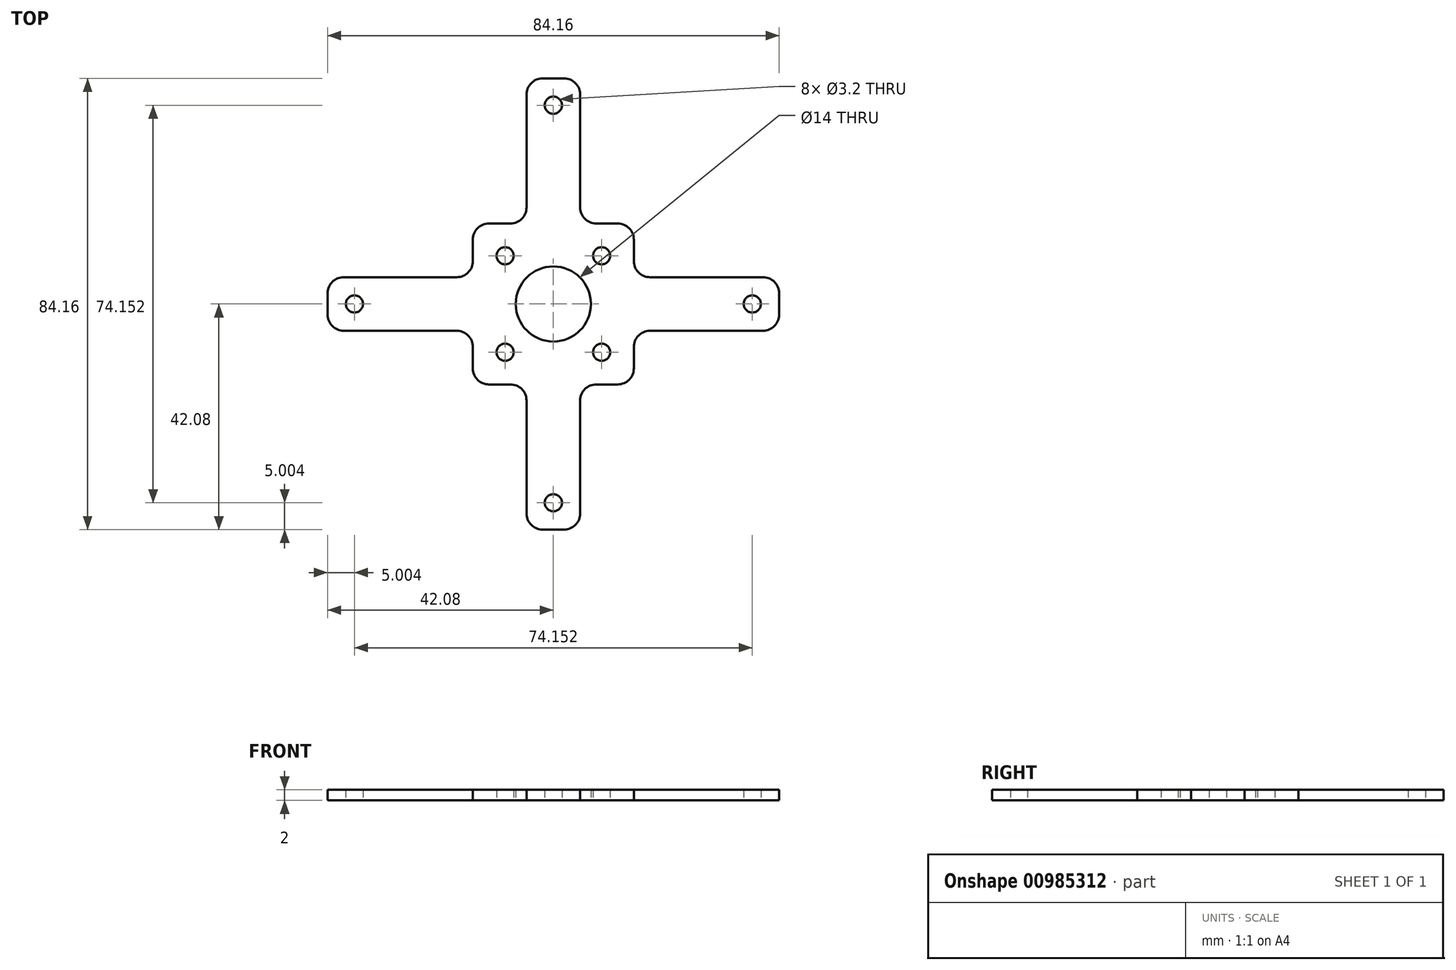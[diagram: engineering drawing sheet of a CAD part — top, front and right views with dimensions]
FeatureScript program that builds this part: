
annotation { "Feature Type Name" : "Feature", "Feature Type Description" : "" }
export const myFeature = defineFeature(function(context is Context, id is Id, definition is map)
    precondition{}
    {
        {
            var Q0;
            Q0=qCreatedBy(makeId("Top.planeOp"),FACE);
            var sketch = newSketch(context, id + "F0", { "sketchPlane" : qUnion([Q0])});
            skLineSegment(sketch, "E0.bottom", {"start": v(-12, -15) * mm, "end": v(-8, -15) * mm});
            skLineSegment(sketch, "E0.top", {"start": v(-12, 15) * mm, "end": v(-8, 15) * mm});
            skLineSegment(sketch, "E0.left", {"start": v(-15, -12) * mm, "end": v(-15, -8) * mm});
            skLineSegment(sketch, "E0.right", {"start": v(15, -12) * mm, "end": v(15, -8) * mm});
            skCircle(sketch, "E1", {"center": v(-9, 9) * mm, "radius": 1.6 * mm});
            skCircle(sketch, "E2", {"center": v(-9, -9) * mm, "radius": 1.6 * mm});
            skCircle(sketch, "E3", {"center": v(9, 9) * mm, "radius": 1.6 * mm});
            skCircle(sketch, "E4", {"center": v(9, -9) * mm, "radius": 1.6 * mm});
            skCircle(sketch, "E5", {"center": v(0, 0) * mm, "radius": 7 * mm});
            skCircle(sketch, "E6", {"center": v(0, 0) * mm, "radius": 31.5 * mm, "construction": true});
            skLineSegment(sketch, "E7.top", {"start": v(-2, -42.08) * mm, "end": v(2, -42.08) * mm});
            skLineSegment(sketch, "E7.left", {"start": v(-5, -18) * mm, "end": v(-5, -39.08) * mm});
            skLineSegment(sketch, "E7.right", {"start": v(5, -18) * mm, "end": v(5, -39.08) * mm});
            skPoint(sketch, "E8.visualSharp", {"position": v(-5, -42.08) * mm});
            skArc(sketch, "E8.filletArc", {"start": v(-5, -39.08) * mm, "mid": v(-4.12, -41.2) * mm, "end": v(-2, -42.08) * mm});
            skPoint(sketch, "E9.visualSharp", {"position": v(5, -42.08) * mm});
            skArc(sketch, "E9.filletArc", {"start": v(2, -42.08) * mm, "mid": v(4.12, -41.2) * mm, "end": v(5, -39.08) * mm});
            skLineSegment(sketch, "E10.trimOffspring", {"start": v(8, -15) * mm, "end": v(12, -15) * mm});
            skPoint(sketch, "E11.visualSharp", {"position": v(-5, -15) * mm});
            skArc(sketch, "E11.filletArc", {"start": v(-5, -18) * mm, "mid": v(-5.88, -15.88) * mm, "end": v(-8, -15) * mm});
            skPoint(sketch, "E12.visualSharp", {"position": v(5, -15) * mm});
            skArc(sketch, "E12.filletArc", {"start": v(8, -15) * mm, "mid": v(5.88, -15.88) * mm, "end": v(5, -18) * mm});
            skLineSegment(sketch, "E13.1.0", {"start": v(-42.08, 2) * mm, "end": v(-42.08, -2) * mm});
            skLineSegment(sketch, "E13.1.1", {"start": v(-18, 5) * mm, "end": v(-39.08, 5) * mm});
            skLineSegment(sketch, "E13.1.2", {"start": v(-18, -5) * mm, "end": v(-39.08, -5) * mm});
            skPoint(sketch, "E13.1.3", {"position": v(-42.08, 5) * mm});
            skPoint(sketch, "E13.1.4", {"position": v(-42.08, -5) * mm});
            skArc(sketch, "E13.1.5", {"start": v(-42.08, -2) * mm, "mid": v(-41.2, -4.12) * mm, "end": v(-39.08, -5) * mm});
            skArc(sketch, "E13.1.6", {"start": v(-39.08, 5) * mm, "mid": v(-41.2, 4.12) * mm, "end": v(-42.08, 2) * mm});
            skLineSegment(sketch, "E13.2.0", {"start": v(2, 42.08) * mm, "end": v(-2, 42.08) * mm});
            skLineSegment(sketch, "E13.2.1", {"start": v(5, 18) * mm, "end": v(5, 39.08) * mm});
            skLineSegment(sketch, "E13.2.2", {"start": v(-5, 18) * mm, "end": v(-5, 39.08) * mm});
            skPoint(sketch, "E13.2.3", {"position": v(5, 42.08) * mm});
            skPoint(sketch, "E13.2.4", {"position": v(-5, 42.08) * mm});
            skArc(sketch, "E13.2.5", {"start": v(-2, 42.08) * mm, "mid": v(-4.12, 41.2) * mm, "end": v(-5, 39.08) * mm});
            skArc(sketch, "E13.2.6", {"start": v(5, 39.08) * mm, "mid": v(4.12, 41.2) * mm, "end": v(2, 42.08) * mm});
            skLineSegment(sketch, "E13.3.0", {"start": v(42.08, -2) * mm, "end": v(42.08, 2) * mm});
            skLineSegment(sketch, "E13.3.1", {"start": v(18, -5) * mm, "end": v(39.08, -5) * mm});
            skLineSegment(sketch, "E13.3.2", {"start": v(18, 5) * mm, "end": v(39.08, 5) * mm});
            skPoint(sketch, "E13.3.3", {"position": v(42.08, -5) * mm});
            skPoint(sketch, "E13.3.4", {"position": v(42.08, 5) * mm});
            skArc(sketch, "E13.3.5", {"start": v(42.08, 2) * mm, "mid": v(41.2, 4.12) * mm, "end": v(39.08, 5) * mm});
            skArc(sketch, "E13.3.6", {"start": v(39.08, -5) * mm, "mid": v(41.2, -4.12) * mm, "end": v(42.08, -2) * mm});
            skLineSegment(sketch, "E13.anchor1", {"start": v(0, 0) * mm, "end": v(-2, -42.08) * mm, "construction": true});
            skLineSegment(sketch, "E13.anchor2", {"start": v(0, 0) * mm, "end": v(42.08, -2) * mm, "construction": true});
            skArc(sketch, "E14.1.0", {"start": v(18, -5) * mm, "mid": v(15.88, -5.88) * mm, "end": v(15, -8) * mm});
            skArc(sketch, "E14.1.1", {"start": v(15, 8) * mm, "mid": v(15.88, 5.88) * mm, "end": v(18, 5) * mm});
            skArc(sketch, "E14.2.0", {"start": v(5, 18) * mm, "mid": v(5.88, 15.88) * mm, "end": v(8, 15) * mm});
            skArc(sketch, "E14.2.1", {"start": v(-8, 15) * mm, "mid": v(-5.88, 15.88) * mm, "end": v(-5, 18) * mm});
            skArc(sketch, "E14.3.0", {"start": v(-18, 5) * mm, "mid": v(-15.88, 5.88) * mm, "end": v(-15, 8) * mm});
            skArc(sketch, "E14.3.1", {"start": v(-15, -8) * mm, "mid": v(-15.88, -5.88) * mm, "end": v(-18, -5) * mm});
            skLineSegment(sketch, "E15.trimOffspring", {"start": v(8, 15) * mm, "end": v(12, 15) * mm});
            skLineSegment(sketch, "E16.trimOffspring", {"start": v(-15, 8) * mm, "end": v(-15, 12) * mm});
            skLineSegment(sketch, "E17.trimOffspring", {"start": v(15, 8) * mm, "end": v(15, 12) * mm});
            skCircle(sketch, "E18", {"center": v(-37.08, 0) * mm, "radius": 1.6 * mm});
            skCircle(sketch, "E19.1.0", {"center": v(0, -37.08) * mm, "radius": 1.6 * mm});
            skCircle(sketch, "E19.2.0", {"center": v(37.08, 0) * mm, "radius": 1.6 * mm});
            skCircle(sketch, "E19.3.0", {"center": v(0, 37.08) * mm, "radius": 1.6 * mm});
            skPoint(sketch, "E20.visualSharp", {"position": v(-15, 15) * mm});
            skArc(sketch, "E20.filletArc", {"start": v(-12, 15) * mm, "mid": v(-14.12, 14.12) * mm, "end": v(-15, 12) * mm});
            skPoint(sketch, "E21.visualSharp", {"position": v(-15, -15) * mm});
            skArc(sketch, "E21.filletArc", {"start": v(-15, -12) * mm, "mid": v(-14.12, -14.12) * mm, "end": v(-12, -15) * mm});
            skPoint(sketch, "E22.visualSharp", {"position": v(15, -15) * mm});
            skArc(sketch, "E22.filletArc", {"start": v(12, -15) * mm, "mid": v(14.12, -14.12) * mm, "end": v(15, -12) * mm});
            skPoint(sketch, "E23.visualSharp", {"position": v(15, 15) * mm});
            skArc(sketch, "E23.filletArc", {"start": v(15, 12) * mm, "mid": v(14.12, 14.12) * mm, "end": v(12, 15) * mm});
            skSolve(sketch);
        }
        {
            var Q0;
            Q0=makeQuery(id+"F0.imprint","IMPRINT",FACE,{"disambiguationData":[TD([[makeQuery(id+"F0.imprint","IMPRINT",EDGE,{"derivedFrom":sQuery(id+"F0.wireOp",EDGE,"E0.bottom")}),1.0]])]});
            extrude(context, id + "F1", {"entities" : qUnion([Q0]), "depth" : 2 * mm, "offsetDistance" : 25 * mm});
        }
    });
